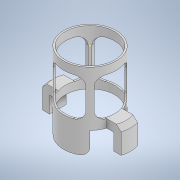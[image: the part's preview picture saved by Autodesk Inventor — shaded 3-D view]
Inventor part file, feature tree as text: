
AUTODESK INVENTOR PART (.ipt)
format: ipt  version: 2020 (Build 240168000, 168)  size: 280,064 bytes
history: native  units: in
note: dims shown in document units (in); Inventor stores cm internally (conversion verified against a paired STEP export)
features: sketch x8, extrude x6, chamfer x2, pattern_circular x1, fillet x1, hole x1, mirror x1
ambient origin geometry x8: Origin, YZ Plane, XZ Plane, XY Plane, X Axis, Y Axis, Z Axis, Center Point
bodies: Solid1 (feature_tree)
feature tree (20):
  extrude  "Extrusion1"  Depth=3.937in TaperAngle=0.0deg
  extrude  "Extrusion2"  Depth=3.937in TaperAngle=0.0deg
  extrude  "Extrusion3"  Depth=2.7559in
  pattern_circular  "Circular Pattern1"  Count=10  [1 undecoded]
  extrude  "Extrusion4"  TaperAngle=45.0deg  [1 undecoded]
  fillet  "Fillet1"  Radius=1.5748in
  extrude  "Extrusion5"  Depth=1.1811in
  chamfer  "Chamfer1"  Distance=1.0236in
  extrude  "Extrusion6"  Depth=0.0787in TaperAngle=0.0deg
  hole  "Hole2"  [1 undecoded]
  mirror  "Mirror1"
  chamfer  "Chamfer2"  Distance=0.315in
  sketch  "Sketch8"  dims[d27=0.1575in d35=0.1575in d36=0.2362in d37=0.1575in d38=0.0787in d39=90.0deg d40=0.2362in d41=0.0in d42=0.315in d43=0.0787in d44=45.0deg d45=0.315in]
  sketch  "Sketch1"  dims[d0=3.7795in d1=3.937in d2=0.0in]
  sketch  "Sketch2"  dims[d3=3.5433in d4=3.937in d5=0.0in]
  sketch  "Sketch3"  dims[d6=2.3622in d7=2.7559in]
  sketch  "Sketch4"  dims[d8=0.5906in d9=3.937in d10=0.0in]
  sketch  "Sketch5"  dims[d11=1.5748in d12=360.0deg d15=45.0deg d16=1.5748in d17=0.0in]
  sketch  "Sketch6"  dims[d18=0.5512in d19=1.1811in d20=1.0236in d21=0.0in]
  sketch  "Sketch7"  dims[d22=0.315in d23=0.0787in d24=45.0deg d25=1.1811in d26=0.0in]
note: 3 required parameter values undecoded (feature->parameter linkage not recoverable at this tier; creation-order binding heuristic only, values carry confidence <= 0.55)
